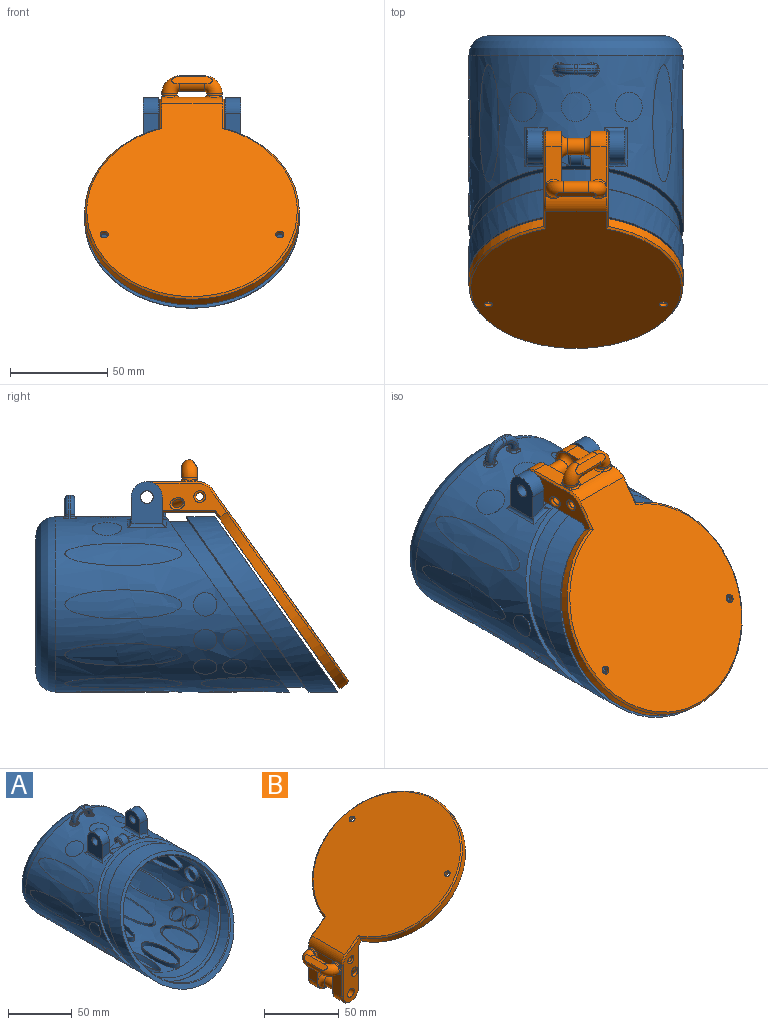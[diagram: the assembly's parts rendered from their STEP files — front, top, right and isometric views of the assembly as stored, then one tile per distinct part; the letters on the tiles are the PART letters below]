
ASSEMBLY  parts=2 mates=1
PART A: 156 faces, bbox 110.3x155.3x108.3 mm
  f0: extruded ~29.1x10mm, area 135.6mm2, adj f1,f2,f3,f4,f5,f6,f7,f8
  f1: plane 3x0.07mm, normal (0,1,0), area 0.1mm2, adj f0,f2,f14
  f2: cylinder r=1mm len=1mm, axis (0,0,-1), area 0.1mm2, adj f0,f1,f3,f15
  f3: plane 8x4.12mm, normal (1,0,0), area 14.8mm2, adj f0,f2,f4,f6,f15
  f4: torus R=2.6mm, axis (1,0,0), area 10mm2, adj f0,f3,f5
  f5: cylinder r=1.6mm len=29.1mm, axis (-1,0,0), area 142mm2, adj f0,f4,f11
  f6: cylinder r=1mm len=1mm, axis (0,0,1), area 0.1mm2, adj f0,f3,f7,f15
  f7: plane 3x0.07mm, normal (0,-1,0), area 0.1mm2, adj f0,f6,f14
  f8: plane 3x0.07mm, normal (0,-1,0), area 0.1mm2, adj f0,f9,f14
  f9: cylinder r=1mm len=1mm, axis (0,0,-1), area 0.1mm2, adj f0,f8,f10,f16
  f10: plane 8x4.12mm, normal (-1,0,0), area 14.8mm2, adj f0,f9,f11,f12,f16
  f11: torus R=2.6mm, axis (1,0,0), area 10mm2, adj f0,f5,f10
  f12: cylinder r=1mm len=1mm, axis (0,0,1), area 0.1mm2, adj f0,f10,f13,f16
  f13: plane 3x0.07mm, normal (0,1,0), area 0.1mm2, adj f0,f12,f14
  f14: cylinder r=5mm len=10mm, axis (1,0,0), area 94.2mm2, adj f0,f1,f7,f8,f13,f15,f16
  f15: torus R=4mm, axis (1,0,0), area 22.9mm2, adj f2,f3,f6,f14
  f16: torus R=4mm, axis (1,0,0), area 22.9mm2, adj f9,f10,f12,f14
  f17: extruded ~7x6.9mm, area 41mm2, adj f18,f19,f20,f21,f22,f23,f24,f25
  f18: bspline ~3.66x3.62mm, area 5.5mm2, adj f17,f19,f25,f26
  f19: cylinder r=1mm len=1mm, axis (0,1,0), area 1.4mm2, adj f17,f18,f20,f27
  f20: bspline ~3.66x3.62mm, area 5.5mm2, adj f17,f19,f21,f28
  f21: bspline ~5.09x1.62mm, area 1.6mm2, adj f17,f20,f22,f29
  f22: bspline ~3.67x3.62mm, area 6mm2, adj f17,f21,f23,f30
  f23: cylinder r=1mm len=1.07mm, axis (0,1,0), area 1.6mm2, adj f17,f22,f24,f31
  f24: bspline ~3.67x3.62mm, area 6mm2, adj f17,f23,f25,f32
  f25: bspline ~5.09x1.62mm, area 1.6mm2, adj f17,f18,f24,f33
  f26: cylinder r=2mm len=2mm, axis (0,0,1), area 2.6mm2, adj f18,f27,f33,f34
  f27: plane 1.07x1mm, normal (-1,0,0), area 1.1mm2, adj f19,f26,f28,f35
  f28: cylinder r=2mm len=2mm, axis (0,0,-1), area 2.6mm2, adj f20,f27,f29,f36
  f29: plane 18x8.6mm, normal (0,1,0), area 26.6mm2, adj f21,f28,f30,f36,f37,f38,f39,f40
  f30: cylinder r=2mm len=2mm, axis (0,0,1), area 1mm2, adj f22,f29,f31,f44
  f31: plane 1x0.18mm, normal (1,0,0), area 0.2mm2, adj f23,f30,f32,f45
  f32: cylinder r=2mm len=2mm, axis (0,0,-1), area 1mm2, adj f24,f31,f33,f46
  f33: plane 18x8.6mm, normal (0,-1,0), area 26.6mm2, adj f25,f26,f32,f34,f46,f47,f48,f49
  f34: torus R=8mm, axis (0,-1,0), area 45.8mm2, adj f26,f33,f35,f51
  f35: cylinder r=10mm len=10mm, axis (0,1,0), area 15.7mm2, adj f27,f34,f36,f54
  f36: torus R=8mm, axis (0,-1,0), area 45.8mm2, adj f28,f29,f35,f37
  f37: cylinder r=2mm len=2mm, axis (-1,0,0), area 6.3mm2, adj f29,f36,f38,f54
  f38: torus R=8mm, axis (0,-1,0), area 45.8mm2, adj f29,f37,f39,f55
  f39: cylinder r=2mm len=2mm, axis (0,0,1), area 2.6mm2, adj f29,f38,f56,f57
  f40: bspline ~5.09x1.62mm, area 1.6mm2, adj f29,f57,f58,f59
  f41: cylinder r=2mm len=2mm, axis (0,0,-1), area 1mm2, adj f29,f42,f58,f60
  f42: torus R=7mm, axis (0,-1,0), area 28.3mm2, adj f29,f41,f43,f61
  f43: cylinder r=2mm len=2mm, axis (1,0,0), area 6.3mm2, adj f29,f42,f44,f62
  f44: torus R=7mm, axis (0,-1,0), area 28.3mm2, adj f29,f30,f43,f45
  f45: cylinder r=5mm len=5mm, axis (0,1,0), area 7.9mm2, adj f31,f44,f46,f62
  f46: torus R=7mm, axis (0,-1,0), area 28.3mm2, adj f32,f33,f45,f52
  f47: cylinder r=2mm len=2mm, axis (0,0,1), area 1mm2, adj f33,f53,f60,f63
  f48: bspline ~5.09x1.62mm, area 1.6mm2, adj f33,f59,f63,f64
  f49: cylinder r=2mm len=2mm, axis (0,0,-1), area 2.6mm2, adj f33,f50,f56,f64
  f50: torus R=8mm, axis (0,-1,0), area 45.8mm2, adj f33,f49,f51,f55
  f51: cylinder r=2mm len=2mm, axis (1,0,0), area 6.3mm2, adj f33,f34,f50,f54
  f52: cylinder r=2mm len=2mm, axis (-1,0,0), area 6.3mm2, adj f33,f46,f53,f62
  f53: torus R=7mm, axis (0,-1,0), area 28.3mm2, adj f33,f47,f52,f61
  f54: plane 2x1mm, normal (0,0,1), area 2mm2, adj f35,f37,f51,f55
  f55: cylinder r=10mm len=10mm, axis (0,1,0), area 15.7mm2, adj f38,f50,f54,f56
  f56: plane 1.07x1mm, normal (1,0,0), area 1.1mm2, adj f39,f49,f55,f65
  f57: bspline ~3.66x3.62mm, area 5.5mm2, adj f39,f40,f59,f65
  f58: bspline ~3.67x3.19mm, area 6mm2, adj f40,f41,f59,f66
  f59: extruded ~7x6.9mm, area 41mm2, adj f40,f48,f57,f58,f63,f64,f65,f66
  f60: plane 1x0.18mm, normal (-1,0,0), area 0.2mm2, adj f41,f47,f61,f66
  f61: cylinder r=5mm len=5mm, axis (0,1,0), area 7.9mm2, adj f42,f53,f60,f62
  f62: plane 2x1mm, normal (0,0,-1), area 2mm2, adj f43,f45,f52,f61
  f63: bspline ~3.67x3.62mm, area 6mm2, adj f47,f48,f59,f66
  f64: bspline ~3.66x3.62mm, area 5.5mm2, adj f48,f49,f59,f65
  f65: cylinder r=1mm len=1mm, axis (0,1,0), area 1.4mm2, adj f56,f57,f59,f64
  f66: cylinder r=1mm len=1.07mm, axis (0,1,0), area 1.6mm2, adj f58,f59,f60,f63
  f67: extruded ~120.01x109.96mm, area 27834.9mm2, adj f68,f69
  f68: plane 110.01x90mm, normal (0,-0.82,0.57), area 868.6mm2, adj f67,f70
  f69: bspline ~110.02x90.03mm, area 4588.3mm2, adj f67,f71
  f70: bspline ~106.01x84.93mm, area 3006.8mm2, adj f68,f72
  f71: plane 90.01x70.02mm, normal (0,1,0), area 3523.2mm2, adj f69,f73,f74,f75,f76
  f72: plane 109.29x89.29mm, normal (0,0.82,-0.57), area 714.1mm2, adj f70,f77
  f73: cylinder r=2.6mm len=5.2mm, axis (0,1,0), area 81.7mm2, adj f71,f78
  f74: cylinder r=2.6mm len=5.2mm, axis (0,1,0), area 81.7mm2, adj f71,f78
  f75: cylinder r=2.6mm len=5.2mm, axis (0,1,0), area 81.7mm2, adj f71,f78
  f76: cylinder r=20.75mm len=41.5mm, axis (0,1,0), area 651.9mm2, adj f71,f78
  f77: bspline ~109.94x89.92mm, area 180.6mm2, adj f72,f79
  f78: plane 82.01x62.02mm, normal (0,-1,0), area 2563.4mm2, adj f73,f74,f75,f76,f80
  f79: extruded ~110x90mm, area 4429mm2, adj f77,f81
  f80: bspline ~101.93x81.87mm, area 4192.9mm2, adj f78,f82,f83
  f81: plane 110.32x90.31mm, normal (0,-0.82,0.57), area 1118.5mm2, adj f79,f84
  f82: extruded ~136.67x102mm, area 43988.3mm2, adj f80,f83,f84,f85,f86,f87,f88,f89
  f83: extruded ~60x16.56mm, area 529mm2, adj f80,f82,f109
  f84: bspline ~104.06x84.06mm, area 443.5mm2, adj f81,f82
  f85: cylinder r=6mm len=12mm, axis (-1,0,0), area 150.8mm2, adj f82,f110
  f86: extruded ~60x15mm, area 522.7mm2, adj f82,f111
  f87: extruded ~60x16.56mm, area 531.7mm2, adj f82,f112
  f88: extruded ~60x16.25mm, area 525.8mm2, adj f82,f113
  f89: extruded ~60x15mm, area 517.3mm2, adj f82,f114
  f90: extruded ~60x16.25mm, area 523.5mm2, adj f82,f115
  f91: extruded ~60x15mm, area 522.7mm2, adj f82,f116
  f92: extruded ~60x16.56mm, area 531.7mm2, adj f82,f117
  f93: extruded ~60x16.56mm, area 529mm2, adj f82,f118
  f94: cylinder r=7.5mm len=16.2mm, axis (0.57,0,-0.82), area 192.4mm2, adj f82,f119
  f95: cylinder r=6mm len=13.47mm, axis (-0.77,0,0.64), area 154.7mm2, adj f82,f120
  f96: cylinder r=6mm len=13.47mm, axis (-0.77,0,0.64), area 154.7mm2, adj f82,f121
  f97: extruded ~40x16.25mm, area 370.3mm2, adj f82,f122
  f98: extruded ~40x16.25mm, area 370.5mm2, adj f82,f123
  f99: extruded ~40x15mm, area 365.2mm2, adj f82,f124
  f100: cylinder r=6mm len=12.64mm, axis (-0.94,0,0.34), area 150.8mm2, adj f82,f125
  f101: cylinder r=6mm len=12.64mm, axis (-0.94,0,0.34), area 150.8mm2, adj f82,f126
  f102: cylinder r=6mm len=12mm, axis (1,0,0), area 153.1mm2, adj f82,f127
  f103: cylinder r=6mm len=12.71mm, axis (0.94,0,0.34), area 158.2mm2, adj f82,f128
  f104: cylinder r=6mm len=13.47mm, axis (0.77,0,0.64), area 154.7mm2, adj f82,f129
  f105: cylinder r=6mm len=12.71mm, axis (0.94,0,0.34), area 158.2mm2, adj f82,f130
  f106: cylinder r=6mm len=13.47mm, axis (0.77,0,0.64), area 154.7mm2, adj f82,f131
  f107: cylinder r=7.5mm len=15mm, axis (0,0,-1), area 189.8mm2, adj f82,f132
  f108: cylinder r=7.5mm len=16.2mm, axis (-0.57,0,-0.82), area 192.4mm2, adj f82,f133
  f109: extruded ~60.01x11.56mm, area 720.8mm2, adj f83
  f110: extruded ~12x12mm, area 113.4mm2, adj f85
  f111: extruded ~60.01x15mm, area 710mm2, adj f86
  f112: extruded ~60.01x11.56mm, area 720.5mm2, adj f87
  f113: extruded ~60.01x14.16mm, area 715.4mm2, adj f88
  f114: extruded ~60.01x15mm, area 707.4mm2, adj f89
  f115: extruded ~60.01x14.16mm, area 715.7mm2, adj f90
  f116: extruded ~60.01x15mm, area 710mm2, adj f91
  f117: extruded ~60.01x11.56mm, area 720.5mm2, adj f92
  f118: extruded ~60.01x11.56mm, area 720.8mm2, adj f93
  f119: extruded ~15x13.79mm, area 179.8mm2, adj f94
  f120: extruded ~12x9.57mm, area 115.6mm2, adj f95
  f121: extruded ~12x9.57mm, area 115.6mm2, adj f96
  f122: extruded ~40.01x14.16mm, area 477.9mm2, adj f97
  f123: extruded ~40x14.16mm, area 477.8mm2, adj f98
  f124: extruded ~40.01x15mm, area 472.1mm2, adj f99
  f125: extruded ~12x10.66mm, area 114.7mm2, adj f100
  f126: extruded ~12x10.66mm, area 114.7mm2, adj f101
  f127: extruded ~12x12mm, area 113.5mm2, adj f102
  f128: extruded ~12x10.66mm, area 114.7mm2, adj f103
  f129: extruded ~12x9.57mm, area 115.6mm2, adj f104
  f130: extruded ~12x10.66mm, area 114.7mm2, adj f105
  f131: extruded ~12x9.57mm, area 115.6mm2, adj f106
  f132: extruded ~15x15mm, area 177mm2, adj f107
  f133: extruded ~15x13.79mm, area 179.8mm2, adj f108
  f134: extruded ~20x11.63mm, area 245.2mm2, adj f135,f136,f137,f138
  f135: cylinder r=2mm len=20mm, axis (0,1,0), area 61.8mm2, adj f134,f136,f138,f139,f140,f141
  f136: bspline ~22.93x9.03mm, area 32.1mm2, adj f134,f135,f137,f141,f142
  f137: cylinder r=2mm len=20mm, axis (0,1,0), area 41.9mm2, adj f134,f136,f138,f142
  f138: bspline ~18.85x8.2mm, area 32.1mm2, adj f134,f135,f137,f139,f142
  f139: plane 12.76x8.07mm, normal (0,1,0), area 90.8mm2, adj f135,f138,f140,f142,f143
  f140: plane 17.65x16mm, normal (1,0,0), area 220.8mm2, adj f135,f139,f141,f143,f144
  f141: plane 12.76x8.07mm, normal (0,-1,0), area 90.8mm2, adj f135,f136,f140,f142,f143
  f142: plane 21.62x16.34mm, normal (-1,0,0), area 284mm2, adj f136,f137,f138,f139,f141,f143,f144
  f143: cylinder r=8mm len=16mm, axis (1,0,0), area 201.1mm2, adj f139,f140,f141,f142
  f144: cylinder r=3.3mm len=8mm, axis (-1,0,0), area 165.9mm2, adj f140,f142
  f145: extruded ~20x11.63mm, area 245.2mm2, adj f146,f147,f148,f149
  f146: cylinder r=2mm len=20mm, axis (0,1,0), area 41.9mm2, adj f145,f147,f149,f150
  f147: bspline ~22.93x9.03mm, area 32.1mm2, adj f145,f146,f148,f150,f151
  f148: cylinder r=2mm len=20mm, axis (0,1,0), area 61.8mm2, adj f145,f147,f149,f151,f152,f153
  f149: bspline ~18.85x8.2mm, area 32.1mm2, adj f145,f146,f148,f150,f153
  f150: plane 21.62x16.34mm, normal (1,0,0), area 284mm2, adj f146,f147,f149,f151,f153,f154,f155
  f151: plane 12.76x8.07mm, normal (0,-1,0), area 90.8mm2, adj f147,f148,f150,f152,f155
  f152: plane 17.65x16mm, normal (-1,0,0), area 220.8mm2, adj f148,f151,f153,f154,f155
  f153: plane 12.76x8.07mm, normal (0,1,0), area 90.8mm2, adj f148,f149,f150,f152,f155
  f154: cylinder r=3.3mm len=8mm, axis (1,0,0), area 165.9mm2, adj f150,f152
  f155: cylinder r=8mm len=16mm, axis (1,0,0), area 201.1mm2, adj f150,f151,f152,f153
PART B: 70 faces, bbox 119.3x110.6x113.6 mm
  f0: cylinder r=2.1mm len=4.59mm, axis (-0.57,0,0.82), area 26.4mm2, adj f8,f65
  f1: cylinder r=2.1mm len=4.59mm, axis (-0.57,0,0.82), area 26.4mm2, adj f8,f63
  f2: cylinder r=10mm len=31mm, axis (0,-1,0), area 243.3mm2, adj f3,f4,f8,f12,f13,f14,f50,f55
  f3: cone r=9mm half-angle=45deg, axis (0,1,0), area 14.9mm2, adj f2,f8,f17,f24,f25
  f4: cone r=9mm half-angle=45deg, axis (0,-1,0), area 14.9mm2, adj f2,f8,f16,f30,f31
  f5: torus R=5mm, axis (0,0,-1), area 182.8mm2, adj f6,f46,f61
  f6: cylinder r=4mm len=13mm, axis (0,1,0), area 266.8mm2, adj f5,f7,f61
  f7: torus R=5mm, axis (0,0,-1), area 182.7mm2, adj f6,f47,f61
  f8: plane 108.31x99.86mm, normal (-0.57,0,0.82), area 9576.3mm2, adj f0,f1,f2,f3,f4,f24,f30,f36
  f9: plane 110x90.5mm, normal (0.57,0,-0.82), area 9427.5mm2, adj f22,f23,f29,f35,f68,f69
  f10: plane 26x16mm, normal (0,-1,0), area 187.4mm2, adj f13,f15,f18,f20,f40,f59
  f11: plane 26x16mm, normal (0,1,0), area 187.4mm2, adj f13,f15,f18,f19,f43,f60
  f12: plane 0.93x0.9mm, normal (-1,0,0), area 0.4mm2, adj f2,f25,f49
  f13: plane 31x25.85mm, normal (-1,0,0), area 390.8mm2, adj f2,f10,f11,f15,f19,f20,f25,f31
  f14: plane 0.93x0.9mm, normal (-1,0,0), area 0.4mm2, adj f2,f31,f54
  f15: plane 16x15mm, normal (0,0,-1), area 240mm2, adj f10,f11,f13,f18
  f16: plane 47.92x17.32mm, normal (0,1,0), area 481.9mm2, adj f4,f21,f22,f30,f31,f32,f33,f34
  f17: plane 47.92x17.32mm, normal (0,-1,0), area 481.9mm2, adj f3,f21,f22,f24,f25,f26,f27,f28
  f18: plane 34.37x31.1mm, normal (1,0,0), area 792.7mm2, adj f10,f11,f15,f19,f20,f23,f27,f33
  f19: cylinder r=8mm len=16mm, axis (0,-1,0), area 201.1mm2, adj f11,f13,f18,f26
  f20: cylinder r=8mm len=16mm, axis (0,-1,0), area 201.1mm2, adj f10,f13,f18,f32
  f21: cylinder r=3.25mm len=33mm, axis (0,1,0), area 673.9mm2, adj f16,f17
  f22: cylinder r=55mm len=110mm, axis (0.57,0,-0.82), area 1561.3mm2, adj f9,f16,f17,f29,f35,f36
  f23: cylinder r=1mm len=31mm, axis (0,1,0), area 29.8mm2, adj f9,f18,f28,f34
  f24: plane 10.52x8.23mm, normal (-0.41,-0.71,0.58), area 17.7mm2, adj f3,f8,f17,f36
  f25: plane 26.46x1.61mm, normal (-0.71,-0.71,0), area 36.6mm2, adj f3,f12,f13,f17,f26,f48,f51
  f26: cone r=7mm half-angle=45deg, axis (0,1,0), area 33.3mm2, adj f17,f19,f25,f27
  f27: plane 34.28x1mm, normal (0.71,-0.71,0), area 48.5mm2, adj f17,f18,f26,f28
  f28: cone r=2mm half-angle=45deg, axis (0,-1,0), area 2mm2, adj f17,f23,f27,f29
  f29: plane 2.79x2.55mm, normal (0.41,-0.71,-0.58), area 4mm2, adj f9,f17,f22,f28
  f30: plane 10.52x8.23mm, normal (-0.41,0.71,0.58), area 17.7mm2, adj f4,f8,f16,f36
  f31: plane 26.46x1.61mm, normal (-0.71,0.71,0), area 36.6mm2, adj f4,f13,f14,f16,f32,f53,f56
  f32: cone r=7mm half-angle=45deg, axis (0,-1,0), area 33.3mm2, adj f16,f20,f31,f33
  f33: plane 34.28x1mm, normal (0.71,0.71,0), area 48.5mm2, adj f16,f18,f32,f34
  f34: cone r=2mm half-angle=45deg, axis (0,1,0), area 2mm2, adj f16,f23,f33,f35
  f35: plane 2.79x2.55mm, normal (0.41,0.71,-0.58), area 4mm2, adj f9,f16,f22,f34
  f36: cone r=55mm half-angle=45deg, axis (0.57,0,-0.82), area 438.3mm2, adj f8,f22,f24,f30
  f37: cylinder r=2mm len=31mm, axis (0,-1,0), area 389.6mm2, adj f44,f45
  f38: cylinder r=2mm len=13.22mm, axis (0.17,0.79,-0.59), area 112mm2, adj f42,f43
  f39: cylinder r=2mm len=13.22mm, axis (0.17,-0.79,-0.59), area 112mm2, adj f40,f41
  f40: bspline ~7.52x6.14mm, area 27.5mm2, adj f10,f18,f39
  f41: bspline ~7.52x6.14mm, area 27.5mm2, adj f16,f39
  f42: bspline ~7.52x6.14mm, area 27.5mm2, adj f17,f38
  f43: bspline ~7.52x6.14mm, area 27.5mm2, adj f11,f18,f38
  f44: torus R=3mm, axis (0,1,0), area 23.3mm2, adj f16,f37
  f45: torus R=3mm, axis (0,-1,0), area 23.3mm2, adj f17,f37
  f46: cylinder r=4mm len=8mm, axis (-1,0,0), area 27.7mm2, adj f5,f48,f49,f50,f51,f52
  f47: cylinder r=4mm len=8mm, axis (1,0,0), area 27.7mm2, adj f7,f53,f54,f55,f56,f57
  f48: bspline ~3.09x1.05mm, area 1.3mm2, adj f25,f46,f49
  f49: torus R=5mm, axis (1,0,0), area 1.8mm2, adj f12,f46,f48,f50
  f50: bspline ~7.73x2.36mm, area 8.7mm2, adj f2,f46,f49,f52
  f51: bspline ~3.09x1.05mm, area 1.3mm2, adj f25,f46,f52
  f52: torus R=5mm, axis (1,0,0), area 23.3mm2, adj f13,f46,f50,f51
  f53: bspline ~3.09x1.05mm, area 1.3mm2, adj f31,f47,f54
  f54: torus R=5mm, axis (1,0,0), area 1.8mm2, adj f14,f47,f53,f55
  f55: bspline ~7.73x2.36mm, area 8.7mm2, adj f2,f47,f54,f57
  f56: bspline ~3.09x1.05mm, area 1.3mm2, adj f31,f47,f57
  f57: torus R=5mm, axis (1,0,0), area 23.3mm2, adj f13,f47,f55,f56
  f58: cylinder r=4.25mm len=9mm, axis (0,-1,0), area 240.3mm2, adj f59,f60
  f59: torus R=7.25mm, axis (0,-1,0), area 158.1mm2, adj f10,f58
  f60: torus R=7.25mm, axis (0,1,0), area 158.1mm2, adj f11,f58
  f61: plane 20.86x3.57mm, normal (-0.57,0,0.82), area 84.4mm2, adj f5,f6,f7
  f62: cylinder r=3.75mm len=7.86mm, axis (0.57,0,-0.82), area 70.7mm2, adj f67,f69
  f63: plane 6.5x5.32mm, normal (0.57,0,-0.82), area 19.3mm2, adj f1,f67
  f64: cylinder r=3.75mm len=7.86mm, axis (0.57,0,-0.82), area 70.7mm2, adj f66,f68
  f65: plane 6.5x5.32mm, normal (0.57,0,-0.82), area 19.3mm2, adj f0,f66
  f66: torus R=3.25mm, axis (0.57,0,-0.82), area 17.6mm2, adj f64,f65
  f67: torus R=3.25mm, axis (0.57,0,-0.82), area 17.6mm2, adj f62,f63
  f68: cone r=3.75mm half-angle=45deg, axis (0.57,0,-0.82), area 17.8mm2, adj f9,f64
  f69: cone r=3.75mm half-angle=45deg, axis (0.57,0,-0.82), area 17.8mm2, adj f9,f62
PLACE A t=(-13.47,-30.4,4.16)mm fixed
PLACE B rot(axis=(0.58,0.58,-0.58),119.8deg) t=(-13.47,-100.35,67.27)mm
MATE revolute B.f19 <-> A.f143  axis (1,0,0) through (3.03,-82.4,59.16)mm
